# Revit family: Контроллер регистрации PERCo_CR01.2 CR01.9
name_source: partatom
category: Охранная сигнализация
units: mm (PartAtom-declared; Revit-internal decimal feet)

## family parameters
Общий = Нет
Основа = Грань
При загрузке вырезать с полостями = Нет
Размер круглого соединителя = Использовать диаметр
Сохранять ориентацию аннотаций = Да
Тип детали = Нормальный
Точка расчета площади = Нет

## types (2) — shared parameters
ADSK_URL страницы изделия = https://www.perco.ru
ADSK_Единица измерения = шт.
ADSK_Завод-изготовитель = PERCo
ADSK_Количество = 1
ADSK_Масса_Текст = не более 0,55 кг
ADSK_Материал наименование = Корпус выполнен из ударопрочного АБС-пластика, с ЖК-дисплеем
ADSK_Напряжение = 12 В
ADSK_Номинальная мощность = 3 В·А
ADSK_Ток = 0 А
Габаритные размеры = 190×140×23 мм
Кол-во выносных считывателей = Не предусмотрено
Кол-во контроллеров 2-го уровня = Не предусмотрено
Кол-во подключаемых замков = Не предусмотрено
Кол-во подключаемых турникетов = Не предусмотрено
Кол-во пользователей = до 50 000
Кол-во событий = до 870 000
Материал корпуса = PERCo_Белый
Наличие встроенного считывателя = Да
Наличие сканера отпечатка пальцев = Нет
Отметка по умолчанию = 1500 мм
Подключение к электросети = 220В
Степень защиты оболочки = IP20
Температура использования = от +1°С до +40°С
Тип интерфейса = Ethernet

## per-type parameters (varying)
| type | ADSK_Наименование | ADSK_Наименование краткое | Формат читаемых карт |
| CR01.2 | Контроллер регистрации PERCo-CR01.2 | Контроллер CR01.2 | EMM, HID Prox |
| CR01.9 | Контроллер регистрации PERCo-CR01.9 | Контроллер CR01.9 | Mifare, EMM, HID Prox |
